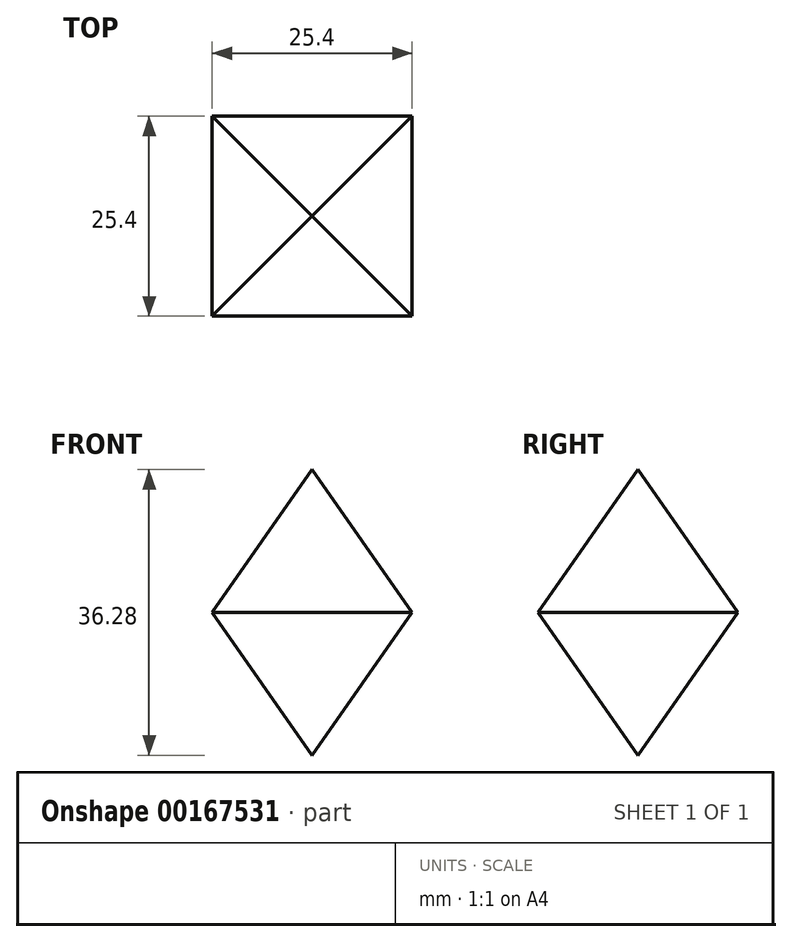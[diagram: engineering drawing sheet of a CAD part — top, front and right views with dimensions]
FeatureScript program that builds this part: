
annotation { "Feature Type Name" : "Feature", "Feature Type Description" : "" }
export const myFeature = defineFeature(function(context is Context, id is Id, definition is map)
    precondition{}
    {
        {
            var Q0;
            Q0=qCreatedBy(makeId("Top.planeOp"),FACE);
            var sketch = newSketch(context, id + "F0", { "sketchPlane" : qUnion([Q0])});
            skLineSegment(sketch, "E0.bottom", {"start": v(12.7, 12.7) * mm, "end": v(-12.7, 12.7) * mm});
            skLineSegment(sketch, "E0.top", {"start": v(12.7, -12.7) * mm, "end": v(-12.7, -12.7) * mm});
            skLineSegment(sketch, "E0.left", {"start": v(12.7, 12.7) * mm, "end": v(12.7, -12.7) * mm});
            skLineSegment(sketch, "E0.right", {"start": v(-12.7, 12.7) * mm, "end": v(-12.7, -12.7) * mm});
            skPoint(sketch, "E0.middle", {"position": v(0, 0) * mm});
            skSolve(sketch);
        }
        {
            var Q0;
            Q0=makeQuery(id+"F0.imprint","IMPRINT",FACE,{"disambiguationData":[TD([[makeQuery(id+"F0.imprint","IMPRINT",EDGE,{"derivedFrom":sQuery(id+"F0.wireOp",EDGE,"E0.bottom")}),1.0]])]});
            extrude(context, id + "F1", {"entities" : qUnion([Q0]), "depth" : 25.4 * mm, "hasDraft" : true, "draftAngle" : 35 * degree, "draftPullDirection" : true});
        }
        {
            var Q0;
            Q0=makeQuery(id+"F1.opExtrude","CAP_FACE",FACE,{"disambiguationData":[OSD([sQuery(id+"F0.wireOp",EDGE,"E0.bottom"),sQuery(id+"F0.wireOp",EDGE,"E0.top"),sQuery(id+"F0.wireOp",EDGE,"E0.left"),sQuery(id+"F0.wireOp",EDGE,"E0.right")])],"isStart":true});
            extrude(context, id + "F2", {"entities" : qUnion([Q0]), "operationType" : NewBodyOperationType.ADD, "depth" : 25.4 * mm, "hasDraft" : true, "draftAngle" : 35 * degree, "draftPullDirection" : true});
        }
    });
